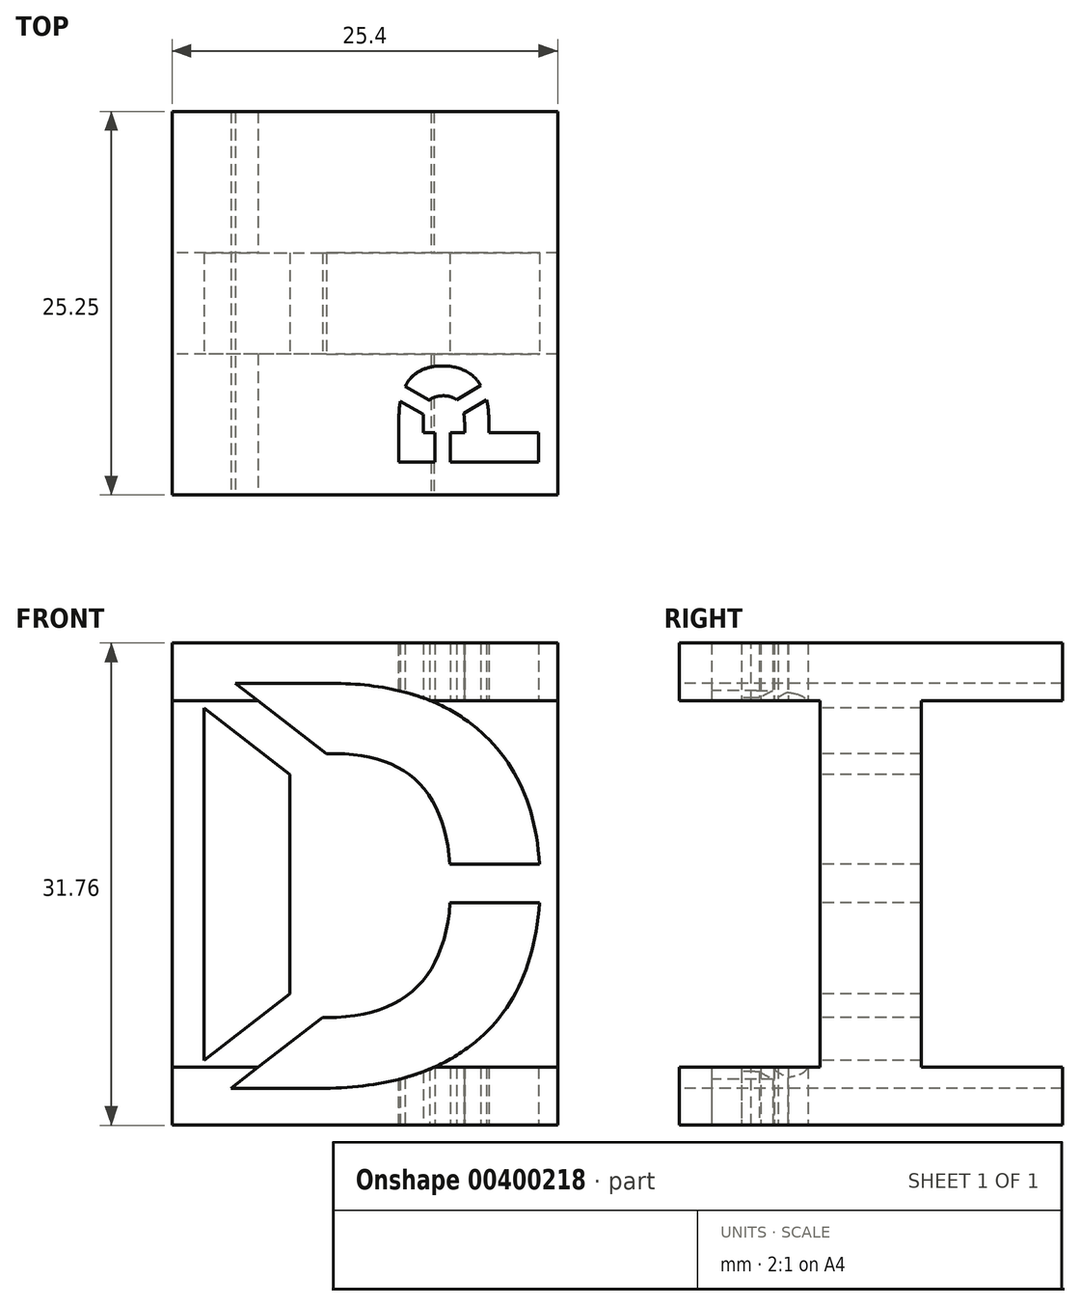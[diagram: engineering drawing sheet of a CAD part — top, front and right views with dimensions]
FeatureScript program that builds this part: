
annotation { "Feature Type Name" : "Feature", "Feature Type Description" : "" }
export const myFeature = defineFeature(function(context is Context, id is Id, definition is map)
    precondition{}
    {
        {
            var Q0;
            Q0=qCreatedBy(makeId("Front.planeOp"),FACE);
            var sketch = newSketch(context, id + "F0", { "sketchPlane" : qUnion([Q0])});
            skLineSegment(sketch, "E0.bottom", {"start": v(12.7, 15.88) * mm, "end": v(-12.7, 15.88) * mm});
            skLineSegment(sketch, "E0.top", {"start": v(12.7, -15.88) * mm, "end": v(-12.7, -15.88) * mm});
            skLineSegment(sketch, "E0.left", {"start": v(12.7, 15.88) * mm, "end": v(12.7, -15.88) * mm});
            skLineSegment(sketch, "E0.right", {"start": v(-12.7, 15.88) * mm, "end": v(-12.7, -15.88) * mm});
            skPoint(sketch, "E0.middle", {"position": v(0, 0) * mm});
            skSolve(sketch);
        }
        {
            var Q0;
            Q0=qSketchRegion(id+"F0",true);
            extrude(context, id + "F1", {"entities" : qUnion([Q0]), "depth" : 31.75 * mm});
        }
        {
            var Q0;
            Q0=makeQuery(id+"F1.opExtrude","SWEPT_FACE",FACE,{"disambiguationData":[OSD([sQuery(id+"F0.wireOp",EDGE,"E0.right")])]});
            var sketch = newSketch(context, id + "F2", { "sketchPlane" : qUnion([Q0])});
            skText(sketch, "E1", { "text": "I", "fontName": "OpenSans-Bold.ttf"});
            skLineSegment(sketch, "E2.bottom", {"start": v(3.25, -15.88) * mm, "end": v(28.5, -15.88) * mm});
            skLineSegment(sketch, "E2.top", {"start": v(3.25, -12.07) * mm, "end": v(28.5, -12.07) * mm});
            skLineSegment(sketch, "E2.left", {"start": v(3.25, -15.88) * mm, "end": v(3.25, -12.07) * mm});
            skLineSegment(sketch, "E2.right", {"start": v(28.5, -15.87) * mm, "end": v(28.5, -12.07) * mm});
            skPoint(sketch, "E3", {"position": v(0, 0) * mm});
            skPoint(sketch, "E4", {"position": v(31.75, 0) * mm});
            skPoint(sketch, "E5", {"position": v(15.88, 15.88) * mm});
            skPoint(sketch, "E6", {"position": v(15.88, -15.88) * mm});
            skLineSegment(sketch, "E7", {"start": v(15.88, 15.88) * mm, "end": v(15.88, -15.88) * mm, "construction": true});
            skPoint(sketch, "E8", {"position": v(15.88, -12.07) * mm});
            skLineSegment(sketch, "E9.bottom", {"start": v(3.25, 15.88) * mm, "end": v(28.5, 15.88) * mm});
            skLineSegment(sketch, "E9.top", {"start": v(3.25, 12.06) * mm, "end": v(28.5, 12.06) * mm});
            skLineSegment(sketch, "E9.left", {"start": v(3.25, 15.87) * mm, "end": v(3.25, 12.06) * mm});
            skLineSegment(sketch, "E9.right", {"start": v(28.5, 15.88) * mm, "end": v(28.5, 12.06) * mm});
            skPoint(sketch, "E10", {"position": v(15.88, 12.06) * mm});
            const initialGuessF2  = {"E1": [0.00858, -0.01588, 1, 0, 0.03175]};
            skSetInitialGuess(sketch, initialGuessF2);
            skSolve(sketch);
        }
        {
            var Q0;
            {var subQ4=sQuery(id+"F2.wireOp",EDGE,"E2.right");Q0=makeQuery(id+"F2.imprint","IMPRINT",FACE,{"disambiguationData":[TD([[makeQuery(id+"F2.imprint","IMPRINT",EDGE,{"derivedFrom":subQ4}),-1.0]])]});}
            var Q1;
            {var subQ0=sQuery(id+"F2.wireOp",EDGE,"E2.left");Q1=makeQuery(id+"F2.imprint","IMPRINT",FACE,{"disambiguationData":[TD([[makeQuery(id+"F2.imprint","IMPRINT",EDGE,{"derivedFrom":subQ0}),1.0]])]});}
            extrude(context, id + "F3", {"entities" : qUnion([Q0, Q1]), "operationType" : NewBodyOperationType.REMOVE, "endBound" : BoundingType.THROUGH_ALL, "oppositeDirection" : true, "depth" : 25.4 * mm});
        }
        {
            var Q0;
            Q0=makeQuery(id+"F3.boolean.opBoolean","COPY",FACE,{"derivedFrom":makeQuery(id+"F3.opExtrude","SWEPT_FACE",FACE,{"disambiguationData":[OSD([sQuery(id+"F2.wireOp",EDGE,"E1.sketch_text.stroke-2")])]})});
            var sketch = newSketch(context, id + "F4", { "sketchPlane" : qUnion([Q0])});
            skText(sketch, "E11", { "text": "D", "fontName": "OpenSans-Bold.ttf"});
            skLineSegment(sketch, "E12.bottom", {"start": v(-10.2, -15.88) * mm, "end": v(9.34, -15.88) * mm, "construction": true});
            skLineSegment(sketch, "E12.top", {"start": v(-10.2, -15.37) * mm, "end": v(9.34, -15.37) * mm, "construction": true});
            skLineSegment(sketch, "E12.left", {"start": v(-10.2, -15.88) * mm, "end": v(-10.2, -15.37) * mm, "construction": true});
            skLineSegment(sketch, "E12.right", {"start": v(9.34, -15.88) * mm, "end": v(9.34, -15.37) * mm, "construction": true});
            skLineSegment(sketch, "E13.bottom", {"start": v(-10.38, -14.66) * mm, "end": v(-2.35, -8.45) * mm});
            skLineSegment(sketch, "E13.top", {"start": v(-11.94, -12.65) * mm, "end": v(-3.9, -6.44) * mm});
            skLineSegment(sketch, "E13.left", {"start": v(-10.38, -14.66) * mm, "end": v(-11.94, -12.65) * mm});
            skLineSegment(sketch, "E13.right", {"start": v(-2.35, -8.45) * mm, "end": v(-3.9, -6.44) * mm});
            skLineSegment(sketch, "E14", {"start": v(0, 0) * mm, "end": v(-36.77, 0) * mm, "construction": true});
            skLineSegment(sketch, "E15.MirrorCS", {"start": v(-10.38, 14.66) * mm, "end": v(-11.94, 12.65) * mm});
            skLineSegment(sketch, "E16.MirrorCS", {"start": v(-11.94, 12.65) * mm, "end": v(-3.9, 6.44) * mm});
            skLineSegment(sketch, "E17.MirrorCS", {"start": v(-10.38, 14.66) * mm, "end": v(-2.35, 8.45) * mm});
            skLineSegment(sketch, "E18.MirrorCS", {"start": v(-2.35, 8.45) * mm, "end": v(-3.9, 6.44) * mm});
            skLineSegment(sketch, "E19.bottom", {"start": v(2.5, -1.24) * mm, "end": v(12.66, -1.23) * mm});
            skLineSegment(sketch, "E19.top", {"start": v(2.5, 1.3) * mm, "end": v(12.66, 1.31) * mm});
            skLineSegment(sketch, "E19.left", {"start": v(2.5, -1.24) * mm, "end": v(2.5, 1.3) * mm});
            skLineSegment(sketch, "E19.right", {"start": v(12.66, -1.23) * mm, "end": v(12.66, 1.31) * mm});
            const initialGuessF4  = {"E11": [-0.01395, -0.01345, 1, 0, 0.0269]};
            skSetInitialGuess(sketch, initialGuessF4);
            skSolve(sketch);
        }
        {
            var Q0;
            {var subQ0=sQuery(id+"F4.wireOp",EDGE,"E11.sketch_text.stroke-5");var subQ1=sQuery(id+"F4.wireOp",EDGE,"E11.sketch_text.stroke-4");var subQ2=makeQuery(id+"F4.imprint","INTERSECT",VERTEX,{"derivedFrom":[subQ1,subQ0]});Q0=makeQuery(id+"F4.imprint","IMPRINT",FACE,{"disambiguationData":[TD([[makeQuery(id+"F4.imprint","IMPRINT",EDGE,{"disambiguationData":[TD([[subQ2,1.0]])],"derivedFrom":subQ1}),-1.0]])]});}
            var Q1;
            {var subQ5=sQuery(id+"F4.wireOp",EDGE,"E11.sketch_text.stroke-5");var subQ10=sQuery(id+"F4.wireOp",EDGE,"E11.sketch_text.stroke-6");var subQ11=makeQuery(id+"F4.imprint","INTERSECT",VERTEX,{"derivedFrom":[subQ5,subQ10]});Q1=makeQuery(id+"F4.imprint","IMPRINT",FACE,{"disambiguationData":[TD([[makeQuery(id+"F4.imprint","IMPRINT",EDGE,{"disambiguationData":[TD([[subQ11,-1.0]])],"derivedFrom":subQ10}),-1.0]])]});}
            var Q2;
            {var subQ5=sQuery(id+"F4.wireOp",EDGE,"E11.sketch_text.stroke-1");var subQ6=sQuery(id+"F4.wireOp",EDGE,"E11.sketch_text.stroke-0");var subQ7=makeQuery(id+"F4.imprint","INTERSECT",VERTEX,{"derivedFrom":[subQ6,subQ5]});Q2=makeQuery(id+"F4.imprint","IMPRINT",FACE,{"disambiguationData":[TD([[makeQuery(id+"F4.imprint","IMPRINT",EDGE,{"disambiguationData":[TD([[subQ7,1.0]])],"derivedFrom":subQ6}),-1.0]])]});}
            var Q3;
            {var subQ0=sQuery(id+"F4.wireOp",EDGE,"E11.sketch_text.stroke-2");var subQ1=sQuery(id+"F4.wireOp",EDGE,"E11.sketch_text.stroke-1");var subQ2=makeQuery(id+"F4.imprint","INTERSECT",VERTEX,{"derivedFrom":[subQ1,subQ0]});Q3=makeQuery(id+"F4.imprint","IMPRINT",FACE,{"disambiguationData":[TD([[makeQuery(id+"F4.imprint","IMPRINT",EDGE,{"disambiguationData":[TD([[subQ2,-1.0]])],"derivedFrom":subQ0}),-1.0]])]});}
            var Q4;
            {var subQ0=sQuery(id+"F4.wireOp",EDGE,"E13.top");var subQ1=sQuery(id+"F4.wireOp",EDGE,"E11.sketch_text.stroke-3");var subQ2=makeQuery(id+"F4.imprint","INTERSECT",VERTEX,{"derivedFrom":[subQ1,subQ0]});Q4=makeQuery(id+"F4.imprint","IMPRINT",FACE,{"disambiguationData":[TD([[makeQuery(id+"F4.imprint","IMPRINT",EDGE,{"disambiguationData":[TD([[subQ2,-1.0]])],"derivedFrom":subQ1}),-1.0]])]});}
            extrude(context, id + "F5", {"entities" : qUnion([Q0, Q1, Q2, Q3, Q4]), "operationType" : NewBodyOperationType.REMOVE, "endBound" : BoundingType.THROUGH_ALL, "oppositeDirection" : true, "offsetDistance" : 25.4 * mm, "depth" : 25.4 * mm, "hasSecondDirection" : true, "secondDirectionBound" : SecondDirectionBoundingType.THROUGH_ALL, "secondDirectionOppositeDirection" : false, "secondDirectionDepth" : 25.4 * mm});
        }
        {
            var Q0;
            {var subQ0=sQuery(id+"F4.wireOp",EDGE,"E12.top");Q0=makeQuery(id+"F5.boolean.opBoolean","MERGE",FACE,{"derivedFrom":[makeQuery(id+"F3.boolean.opBoolean","COPY",FACE,{"derivedFrom":makeQuery(id+"F3.opExtrude","SWEPT_FACE",FACE,{"disambiguationData":[OSD([sQuery(id+"F2.wireOp",EDGE,"E2.top")])]})}),makeQuery(id+"F5.opExtrude","SWEPT_FACE",FACE,{"disambiguationData":[OSD([subQ0]),TDD([makeQuery(id+"F4.imprint","IMPRINT",EDGE,{"disambiguationData":[TD([[makeQuery(id+"F4.imprint","INTERSECT",VERTEX,{"derivedFrom":[subQ0,sQuery(id+"F4.wireOp",EDGE,"E12.left")]}),-1.0]])],"derivedFrom":subQ0})])]}),makeQuery(id+"F5.opExtrude","SWEPT_FACE",FACE,{"disambiguationData":[OSD([subQ0]),TDD([makeQuery(id+"F4.imprint","IMPRINT",EDGE,{"disambiguationData":[TD([[makeQuery(id+"F4.imprint","INTERSECT",VERTEX,{"derivedFrom":[subQ0,sQuery(id+"F4.wireOp",EDGE,"E12.right")]}),1.0]])],"derivedFrom":subQ0})])]})]});}
            var sketch = newSketch(context, id + "F6", { "sketchPlane" : qUnion([Q0])});
            skText(sketch, "E20", { "text": "P", "fontName": "OpenSans-Bold.ttf"});
            skLineSegment(sketch, "E21.bottom", {"start": v(5.62, -23.85) * mm, "end": v(4.6, -23.85) * mm});
            skLineSegment(sketch, "E21.top", {"start": v(5.62, -27.66) * mm, "end": v(4.6, -27.66) * mm});
            skLineSegment(sketch, "E21.left", {"start": v(5.62, -27.66) * mm, "end": v(5.62, -23.85) * mm});
            skLineSegment(sketch, "E21.right", {"start": v(4.6, -27.66) * mm, "end": v(4.6, -23.85) * mm});
            skPoint(sketch, "E22", {"position": v(5.11, -23.34) * mm});
            skLineSegment(sketch, "E23", {"start": v(5.11, -23.34) * mm, "end": v(5.11, -27.5) * mm, "construction": true});
            skPoint(sketch, "E24", {"position": v(5.11, -23.85) * mm});
            skLineSegment(sketch, "E25.1.0", {"start": v(8.6, -20.74) * mm, "end": v(5.3, -22.65) * mm});
            skLineSegment(sketch, "E25.1.1", {"start": v(8.6, -20.74) * mm, "end": v(9.1, -21.62) * mm});
            skLineSegment(sketch, "E25.1.2", {"start": v(9.1, -21.62) * mm, "end": v(5.8, -23.53) * mm});
            skLineSegment(sketch, "E25.1.3", {"start": v(5.3, -22.65) * mm, "end": v(5.8, -23.53) * mm});
            skLineSegment(sketch, "E25.2.0", {"start": v(1.12, -21.62) * mm, "end": v(4.42, -23.53) * mm});
            skLineSegment(sketch, "E25.2.1", {"start": v(1.12, -21.62) * mm, "end": v(1.63, -20.74) * mm});
            skLineSegment(sketch, "E25.2.2", {"start": v(1.63, -20.74) * mm, "end": v(4.93, -22.65) * mm});
            skLineSegment(sketch, "E25.2.3", {"start": v(4.42, -23.53) * mm, "end": v(4.93, -22.65) * mm});
            const initialGuessF6  = {"E20": [0.01143, -0.0275, 0, 1, 0.00926]};
            skSetInitialGuess(sketch, initialGuessF6);
            skSolve(sketch);
        }
        {
            var Q0;
            {var subQ1=sQuery(id+"F6.wireOp",EDGE,"E20.sketch_text.stroke-0");Q0=makeQuery(id+"F6.imprint","IMPRINT",FACE,{"disambiguationData":[TD([[makeQuery(id+"F6.imprint","IMPRINT",EDGE,{"derivedFrom":subQ1}),-1.0]])]});}
            var Q1;
            {var subQ0=sQuery(id+"F6.wireOp",EDGE,"E20.sketch_text.stroke-7");Q1=makeQuery(id+"F6.imprint","IMPRINT",FACE,{"disambiguationData":[TD([[makeQuery(id+"F6.imprint","IMPRINT",EDGE,{"derivedFrom":subQ0}),-1.0]])]});}
            var Q2;
            {var subQ5=sQuery(id+"F6.wireOp",EDGE,"E20.sketch_text.stroke-5");Q2=makeQuery(id+"F6.imprint","IMPRINT",FACE,{"disambiguationData":[TD([[makeQuery(id+"F6.imprint","IMPRINT",EDGE,{"derivedFrom":subQ5}),-1.0]])]});}
            var Q3;
            {var subQ1=sQuery(id+"F6.wireOp",EDGE,"E20.sketch_text.stroke-14");var subQ5=sQuery(id+"F6.wireOp",EDGE,"E20.sketch_text.stroke-15");var subQ6=makeQuery(id+"F6.imprint","INTERSECT",VERTEX,{"derivedFrom":[subQ1,subQ5]});Q3=makeQuery(id+"F6.imprint","IMPRINT",FACE,{"disambiguationData":[TD([[makeQuery(id+"F6.imprint","IMPRINT",EDGE,{"disambiguationData":[TD([[subQ6,1.0]])],"derivedFrom":subQ1}),-1.0]])]});}
            extrude(context, id + "F7", {"entities" : qUnion([Q0, Q1, Q2, Q3]), "operationType" : NewBodyOperationType.REMOVE, "endBound" : BoundingType.THROUGH_ALL, "offsetDistance" : 25.4 * mm, "depth" : 25.4 * mm, "hasSecondDirection" : true, "secondDirectionBound" : SecondDirectionBoundingType.THROUGH_ALL, "secondDirectionOppositeDirection" : true, "secondDirectionDepth" : 25.4 * mm});
        }
    });
